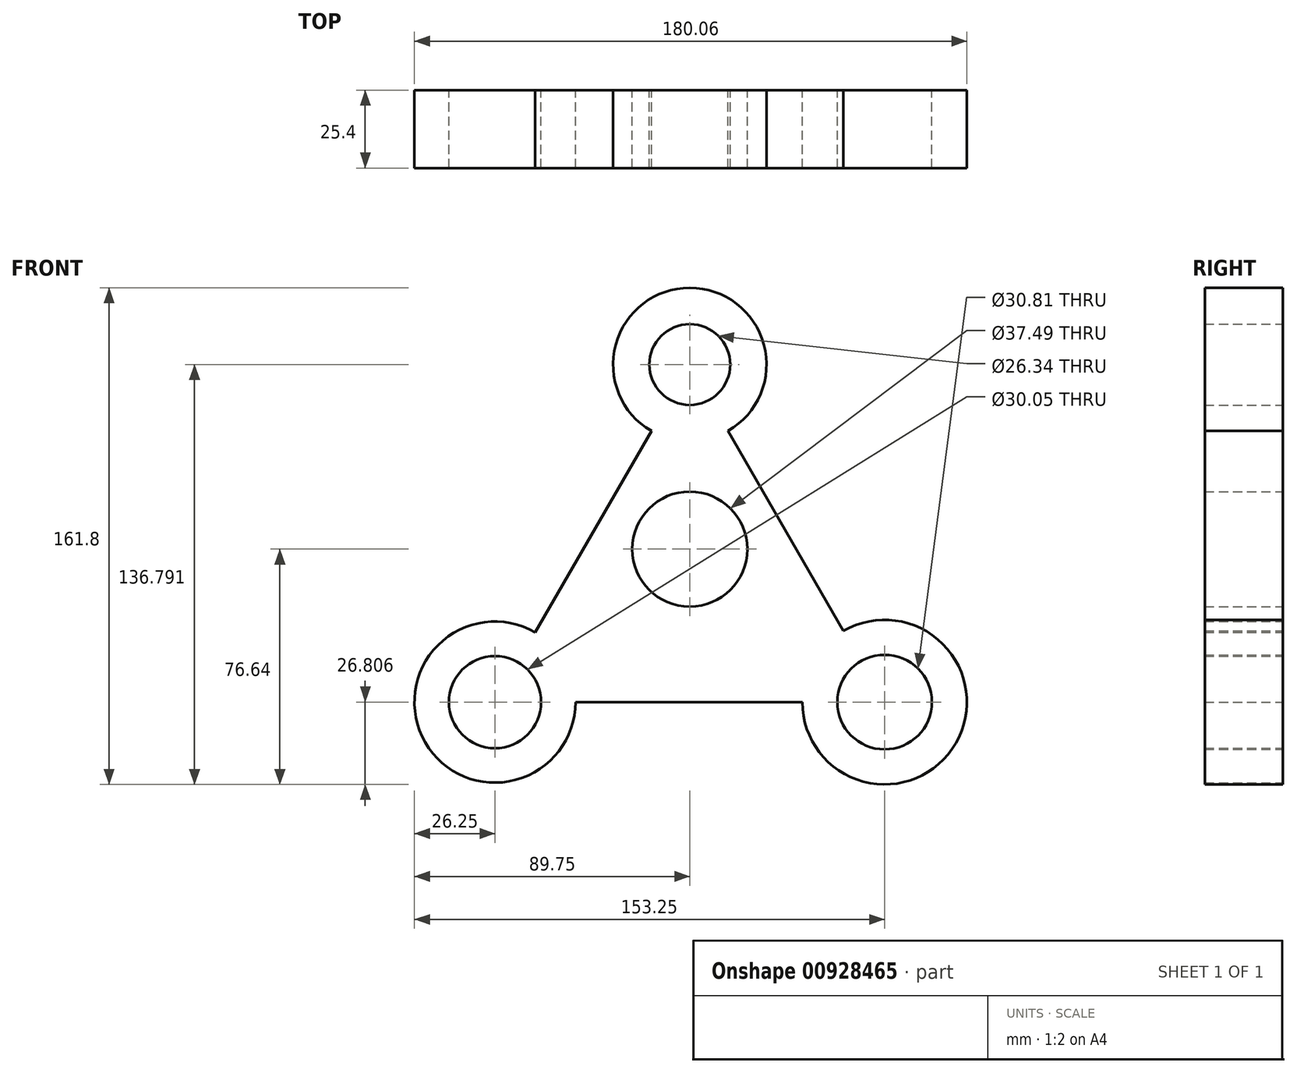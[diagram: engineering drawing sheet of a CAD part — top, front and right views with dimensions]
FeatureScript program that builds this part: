
annotation { "Feature Type Name" : "Feature", "Feature Type Description" : "" }
export const myFeature = defineFeature(function(context is Context, id is Id, definition is map)
    precondition{}
    {
        {
            var Q0;
            Q0=qCreatedBy(makeId("Front.planeOp"),FACE);
            var sketch = newSketch(context, id + "F0", { "sketchPlane" : qUnion([Q0])});
            skLineSegment(sketch, "E0", {"start": v(0, 60.15) * mm, "end": v(-63.5, -49.83) * mm});
            skLineSegment(sketch, "E1", {"start": v(-63.5, -49.83) * mm, "end": v(63.5, -49.83) * mm});
            skLineSegment(sketch, "E2", {"start": v(63.5, -49.83) * mm, "end": v(0, 60.15) * mm});
            skCircle(sketch, "E3", {"center": v(0, 60.15) * mm, "radius": 25 * mm});
            skCircle(sketch, "E4", {"center": v(63.5, -49.83) * mm, "radius": 26.81 * mm});
            skCircle(sketch, "E5", {"center": v(-63.5, -49.83) * mm, "radius": 26.25 * mm});
            skCircle(sketch, "E6", {"center": v(0, 0) * mm, "radius": 18.74 * mm});
            skCircle(sketch, "E7", {"center": v(0, 60.15) * mm, "radius": 13.17 * mm});
            skCircle(sketch, "E8", {"center": v(63.5, -49.83) * mm, "radius": 15.4 * mm});
            skCircle(sketch, "E9", {"center": v(-63.5, -49.83) * mm, "radius": 15.03 * mm});
            skCircle(sketch, "E10", {"center": v(0, 0) * mm, "radius": 9.63 * mm});
            skSolve(sketch);
        }
        {
            var Q0;
            {var subQ0=sQuery(id+"F0.wireOp",EDGE,"E3");var subQ1=sQuery(id+"F0.wireOp",EDGE,"E0");var subQ2=makeQuery(id+"F0.imprint","INTERSECT",VERTEX,{"derivedFrom":[subQ1,subQ0]});Q0=makeQuery(id+"F0.imprint","IMPRINT",FACE,{"disambiguationData":[TD([[makeQuery(id+"F0.imprint","IMPRINT",EDGE,{"disambiguationData":[TD([[subQ2,1.0]])],"derivedFrom":subQ1}),-1.0]])]});}
            var Q1;
            {var subQ0=sQuery(id+"F0.wireOp",EDGE,"E3");var subQ1=sQuery(id+"F0.wireOp",EDGE,"E0");var subQ2=makeQuery(id+"F0.imprint","INTERSECT",VERTEX,{"derivedFrom":[subQ1,subQ0]});Q1=makeQuery(id+"F0.imprint","IMPRINT",FACE,{"disambiguationData":[TD([[makeQuery(id+"F0.imprint","IMPRINT",EDGE,{"disambiguationData":[TD([[subQ2,1.0]])],"derivedFrom":subQ1}),1.0]])]});}
            var Q2;
            Q2=makeQuery(id+"F0.imprint","IMPRINT",FACE,{"disambiguationData":[TD([[makeQuery(id+"F0.imprint","IMPRINT",EDGE,{"derivedFrom":sQuery(id+"F0.wireOp",EDGE,"E6")}),-1.0]])]});
            var Q3;
            {var subQ0=sQuery(id+"F0.wireOp",EDGE,"E4");var subQ1=sQuery(id+"F0.wireOp",EDGE,"E1");var subQ2=makeQuery(id+"F0.imprint","INTERSECT",VERTEX,{"derivedFrom":[subQ1,subQ0]});Q3=makeQuery(id+"F0.imprint","IMPRINT",FACE,{"disambiguationData":[TD([[makeQuery(id+"F0.imprint","IMPRINT",EDGE,{"disambiguationData":[TD([[subQ2,-1.0]])],"derivedFrom":subQ1}),1.0]])]});}
            var Q4;
            {var subQ0=sQuery(id+"F0.wireOp",EDGE,"E4");var subQ1=sQuery(id+"F0.wireOp",EDGE,"E1");var subQ2=makeQuery(id+"F0.imprint","INTERSECT",VERTEX,{"derivedFrom":[subQ1,subQ0]});Q4=makeQuery(id+"F0.imprint","IMPRINT",FACE,{"disambiguationData":[TD([[makeQuery(id+"F0.imprint","IMPRINT",EDGE,{"disambiguationData":[TD([[subQ2,-1.0]])],"derivedFrom":subQ1}),-1.0]])]});}
            var Q5;
            {var subQ0=sQuery(id+"F0.wireOp",EDGE,"E5");var subQ1=sQuery(id+"F0.wireOp",EDGE,"E0");var subQ2=makeQuery(id+"F0.imprint","INTERSECT",VERTEX,{"derivedFrom":[subQ1,subQ0]});Q5=makeQuery(id+"F0.imprint","IMPRINT",FACE,{"disambiguationData":[TD([[makeQuery(id+"F0.imprint","IMPRINT",EDGE,{"disambiguationData":[TD([[subQ2,-1.0]])],"derivedFrom":subQ1}),1.0]])]});}
            var Q6;
            {var subQ0=sQuery(id+"F0.wireOp",EDGE,"E5");var subQ1=sQuery(id+"F0.wireOp",EDGE,"E0");var subQ2=makeQuery(id+"F0.imprint","INTERSECT",VERTEX,{"derivedFrom":[subQ1,subQ0]});Q6=makeQuery(id+"F0.imprint","IMPRINT",FACE,{"disambiguationData":[TD([[makeQuery(id+"F0.imprint","IMPRINT",EDGE,{"disambiguationData":[TD([[subQ2,-1.0]])],"derivedFrom":subQ1}),-1.0]])]});}
            extrude(context, id + "F1", {"entities" : qUnion([Q0, Q1, Q2, Q3, Q4, Q5, Q6]), "depth" : 25.4 * mm, "offsetDistance" : 25.4 * mm});
        }
    });
